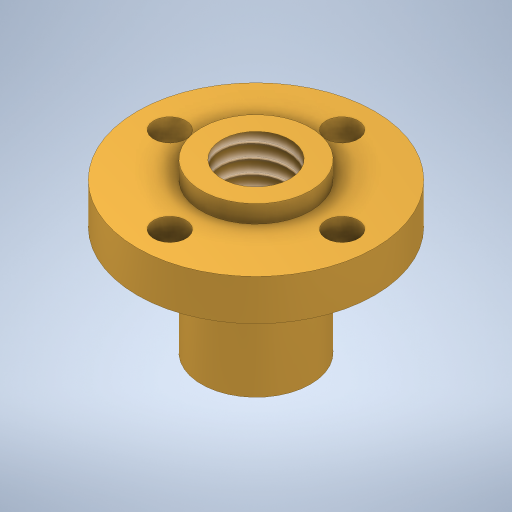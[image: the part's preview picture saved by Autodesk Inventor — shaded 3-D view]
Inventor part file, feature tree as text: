
AUTODESK INVENTOR PART (.ipt)
format: ipt  version: 2024 (Build 280153000, 153)  size: 291,328 bytes
history: native  units: in
note: dims shown in document units (in); Inventor stores cm internally (conversion verified against a paired STEP export)
features: extrude x3, sketch x3, thread x1, projected_geometry x1
ambient origin geometry x8: Origin, YZ Plane, XZ Plane, XY Plane, X Axis, Y Axis, Z Axis, Center Point
bodies: Solid1 (feature_tree)
feature tree (8):
  extrude  "Extrusion1"  Depth=0.25in
  extrude  "Extrusion2"  Depth=0.06in
  extrude  "Extrusion3"  Depth=0.615in TaperAngle=360.0deg
  thread  "Thread1"  [1 undecoded]
  sketch  "Sketch1"  dims[d0=0.87in d1=0.25in]
  sketch  "Sketch2"  dims[d2=0.1181in d3=0.06in]
  sketch  "Sketch3"  dims[d4=0.4in d5=1.5748in d7=360.0deg d9=0.15in d10=0.0in d11=0.4in d12=0.065in d13=0.0in d14=0.4in d15=0.0in d16=0.615in d17=0.0in]
  projected_geometry  "Projected Loop1"
note: 1 required parameter value undecoded (feature->parameter linkage not recoverable at this tier; creation-order binding heuristic only, values carry confidence <= 0.55)
